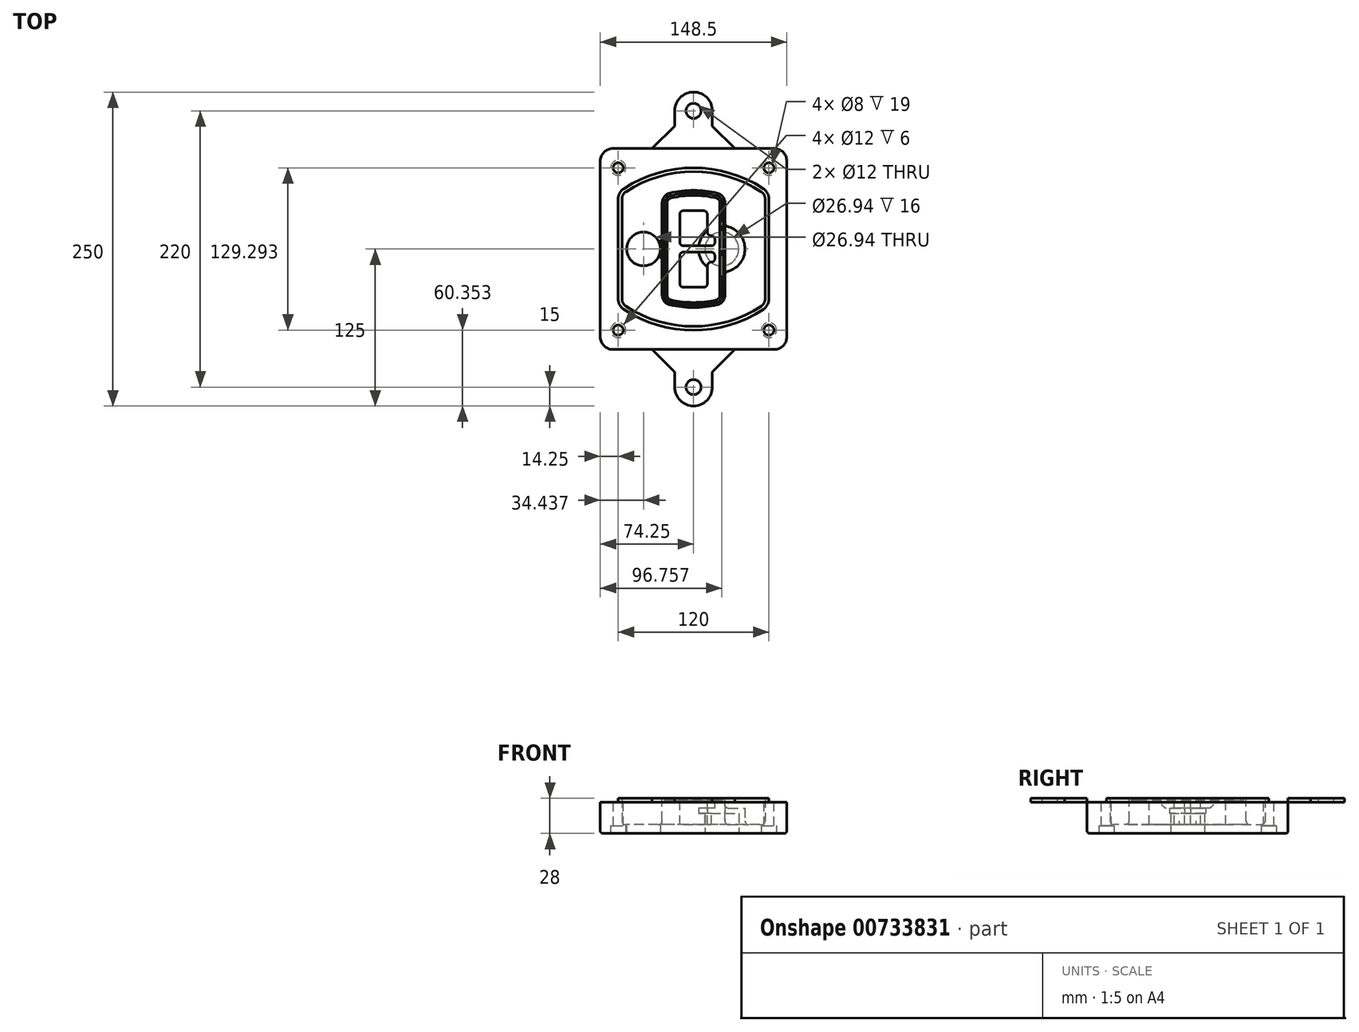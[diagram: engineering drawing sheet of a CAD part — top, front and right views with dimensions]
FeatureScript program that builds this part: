
annotation { "Feature Type Name" : "Feature", "Feature Type Description" : "" }
export const myFeature = defineFeature(function(context is Context, id is Id, definition is map)
    precondition{}
    {
        {
            var Q0;
            Q0=qCreatedBy(makeId("Top.planeOp"),FACE);
            var sketch = newSketch(context, id + "F0", { "sketchPlane" : qUnion([Q0])});
            skPoint(sketch, "E0.rect.middle", {"position": v(0, 0) * mm});
            skLineSegment(sketch, "E1.bottom", {"start": v(-64.25, -80) * mm, "end": v(64.25, -80) * mm});
            skLineSegment(sketch, "E1.top", {"start": v(-64.25, 80) * mm, "end": v(64.25, 80) * mm});
            skLineSegment(sketch, "E1.left", {"start": v(-74.25, -70) * mm, "end": v(-74.25, 70) * mm});
            skLineSegment(sketch, "E1.right", {"start": v(74.25, -70) * mm, "end": v(74.25, 70) * mm});
            skLineSegment(sketch, "E2", {"start": v(-74.25, 80) * mm, "end": v(74.25, -80) * mm, "construction": true});
            skLineSegment(sketch, "E3", {"start": v(74.25, 80) * mm, "end": v(-74.25, -80) * mm, "construction": true});
            skCircle(sketch, "E4", {"center": v(-60, 64.65) * mm, "radius": 4 * mm});
            skCircle(sketch, "E5", {"center": v(60, 64.65) * mm, "radius": 4 * mm});
            skCircle(sketch, "E6", {"center": v(60, -64.65) * mm, "radius": 4 * mm});
            skCircle(sketch, "E7", {"center": v(-60, -64.65) * mm, "radius": 4 * mm});
            skLineSegment(sketch, "E8", {"start": v(-60, 64.65) * mm, "end": v(60, 64.65) * mm, "construction": true});
            skLineSegment(sketch, "E9", {"start": v(60, 64.65) * mm, "end": v(60, -64.65) * mm, "construction": true});
            skLineSegment(sketch, "E10", {"start": v(60, -64.65) * mm, "end": v(-60, -64.65) * mm, "construction": true});
            skLineSegment(sketch, "E11", {"start": v(-60, -64.65) * mm, "end": v(-60, 64.65) * mm, "construction": true});
            skLineSegment(sketch, "E12", {"start": v(-60, 39.77) * mm, "end": v(-60, -39.77) * mm});
            skLineSegment(sketch, "E13", {"start": v(60, 39.77) * mm, "end": v(60, -39.77) * mm});
            skArc(sketch, "E14", {"start": v(55.47, 48.14) * mm, "mid": v(0, 64.65) * mm, "end": v(-55.47, 48.14) * mm});
            skArc(sketch, "E15", {"start": v(-55.47, -48.14) * mm, "mid": v(0, -64.65) * mm, "end": v(55.47, -48.14) * mm});
            skLineSegment(sketch, "E16", {"start": v(-60, 0) * mm, "end": v(60, 0) * mm, "construction": true});
            skPoint(sketch, "E17.visualSharp", {"position": v(-60, -45) * mm});
            skArc(sketch, "E17.filletArc", {"start": v(-60, -39.77) * mm, "mid": v(-58.8, -44.53) * mm, "end": v(-55.47, -48.14) * mm});
            skPoint(sketch, "E18.visualSharp", {"position": v(-60, 45) * mm});
            skArc(sketch, "E18.filletArc", {"start": v(-55.47, 48.14) * mm, "mid": v(-58.8, 44.53) * mm, "end": v(-60, 39.77) * mm});
            skPoint(sketch, "E19.visualSharp", {"position": v(60, 45) * mm});
            skArc(sketch, "E19.filletArc", {"start": v(60, 39.77) * mm, "mid": v(58.8, 44.53) * mm, "end": v(55.47, 48.14) * mm});
            skPoint(sketch, "E20.visualSharp", {"position": v(60, -45) * mm});
            skArc(sketch, "E20.filletArc", {"start": v(55.47, -48.14) * mm, "mid": v(58.8, -44.53) * mm, "end": v(60, -39.77) * mm});
            skPoint(sketch, "E21.visualSharp", {"position": v(-74.25, 80) * mm});
            skArc(sketch, "E21.filletArc", {"start": v(-64.25, 80) * mm, "mid": v(-71.32, 77.07) * mm, "end": v(-74.25, 70) * mm});
            skPoint(sketch, "E22.visualSharp", {"position": v(74.25, 80) * mm});
            skArc(sketch, "E22.filletArc", {"start": v(74.25, 70) * mm, "mid": v(71.32, 77.07) * mm, "end": v(64.25, 80) * mm});
            skPoint(sketch, "E23.visualSharp", {"position": v(74.25, -80) * mm});
            skArc(sketch, "E23.filletArc", {"start": v(64.25, -80) * mm, "mid": v(71.32, -77.07) * mm, "end": v(74.25, -70) * mm});
            skPoint(sketch, "E24.visualSharp", {"position": v(-74.25, -80) * mm});
            skArc(sketch, "E24.filletArc", {"start": v(-74.25, -70) * mm, "mid": v(-71.32, -77.07) * mm, "end": v(-64.25, -80) * mm});
            skArc(sketch, "E25.0", {"start": v(57, 39.77) * mm, "mid": v(56.16, 43.1) * mm, "end": v(53.83, 45.63) * mm});
            skLineSegment(sketch, "E25.1", {"start": v(57, 39.77) * mm, "end": v(57, -39.77) * mm});
            skArc(sketch, "E25.2", {"start": v(53.83, -45.63) * mm, "mid": v(56.16, -43.1) * mm, "end": v(57, -39.77) * mm});
            skArc(sketch, "E25.3", {"start": v(-53.83, -45.63) * mm, "mid": v(0, -61.65) * mm, "end": v(53.83, -45.63) * mm});
            skArc(sketch, "E25.4", {"start": v(-57, -39.77) * mm, "mid": v(-56.16, -43.1) * mm, "end": v(-53.83, -45.63) * mm});
            skArc(sketch, "E25.5", {"start": v(53.83, 45.63) * mm, "mid": v(0, 61.65) * mm, "end": v(-53.83, 45.63) * mm});
            skLineSegment(sketch, "E25.6", {"start": v(-57, 39.77) * mm, "end": v(-57, -39.77) * mm});
            skArc(sketch, "E25.7", {"start": v(-53.83, 45.63) * mm, "mid": v(-56.16, 43.1) * mm, "end": v(-57, 39.77) * mm});
            skArc(sketch, "E26.0", {"start": v(-57.66, 51.49) * mm, "mid": v(-62.31, 46.43) * mm, "end": v(-64, 39.77) * mm});
            skArc(sketch, "E26.1", {"start": v(57.66, 51.49) * mm, "mid": v(0, 68.65) * mm, "end": v(-57.66, 51.49) * mm});
            skArc(sketch, "E26.2", {"start": v(64, 39.77) * mm, "mid": v(62.31, 46.43) * mm, "end": v(57.66, 51.49) * mm});
            skLineSegment(sketch, "E26.3", {"start": v(64, 39.77) * mm, "end": v(64, -39.77) * mm});
            skArc(sketch, "E26.4", {"start": v(57.66, -51.49) * mm, "mid": v(62.31, -46.43) * mm, "end": v(64, -39.77) * mm});
            skLineSegment(sketch, "E26.5", {"start": v(-64, 39.77) * mm, "end": v(-64, -39.77) * mm});
            skArc(sketch, "E26.6", {"start": v(-57.66, -51.49) * mm, "mid": v(0, -68.65) * mm, "end": v(57.66, -51.49) * mm});
            skArc(sketch, "E26.7", {"start": v(-64, -39.77) * mm, "mid": v(-62.31, -46.43) * mm, "end": v(-57.66, -51.49) * mm});
            skSolve(sketch);
        }
        {
            var Q0;
            Q0=makeQuery(id+"F0.imprint","IMPRINT",FACE,{"disambiguationData":[TD([[makeQuery(id+"F0.imprint","IMPRINT",EDGE,{"derivedFrom":sQuery(id+"F0.wireOp",EDGE,"E1.bottom")}),1.0]])]});
            var Q1;
            Q1=makeQuery(id+"F0.imprint","IMPRINT",FACE,{"disambiguationData":[TD([[makeQuery(id+"F0.imprint","IMPRINT",EDGE,{"derivedFrom":sQuery(id+"F0.wireOp",EDGE,"E12")}),1.0]])]});
            var Q2;
            Q2=makeQuery(id+"F0.imprint","IMPRINT",FACE,{"disambiguationData":[TD([[makeQuery(id+"F0.imprint","IMPRINT",EDGE,{"derivedFrom":sQuery(id+"F0.wireOp",EDGE,"E25.0")}),1.0]])]});
            var Q3;
            Q3=makeQuery(id+"F0.imprint","IMPRINT",FACE,{"disambiguationData":[TD([[makeQuery(id+"F0.imprint","IMPRINT",EDGE,{"derivedFrom":sQuery(id+"F0.wireOp",EDGE,"E12")}),-1.0]])]});
            extrude(context, id + "F1", {"entities" : qUnion([Q0, Q1, Q2, Q3]), "oppositeDirection" : true, "depth" : 25 * mm});
        }
        {
            var Q0;
            Q0=makeQuery(id+"F0.imprint","IMPRINT",FACE,{"disambiguationData":[TD([[makeQuery(id+"F0.imprint","IMPRINT",EDGE,{"derivedFrom":sQuery(id+"F0.wireOp",EDGE,"E12")}),1.0]])]});
            extrude(context, id + "F2", {"entities" : qUnion([Q0]), "operationType" : NewBodyOperationType.ADD, "depth" : 3 * mm});
        }
        {
            var Q0;
            Q0=makeQuery(id+"F0.imprint","IMPRINT",FACE,{"disambiguationData":[TD([[makeQuery(id+"F0.imprint","IMPRINT",EDGE,{"derivedFrom":sQuery(id+"F0.wireOp",EDGE,"E25.0")}),1.0]])]});
            extrude(context, id + "F3", {"entities" : qUnion([Q0]), "operationType" : NewBodyOperationType.REMOVE, "oppositeDirection" : true, "depth" : 18 * mm});
        }
        {
            var Q0;
            Q0=makeQuery(id+"F2.opExtrude","CAP_FACE",FACE,{"disambiguationData":[OSD([sQuery(id+"F0.wireOp",EDGE,"E12"),sQuery(id+"F0.wireOp",EDGE,"E13"),sQuery(id+"F0.wireOp",EDGE,"E14"),sQuery(id+"F0.wireOp",EDGE,"E15"),sQuery(id+"F0.wireOp",EDGE,"E17.filletArc"),sQuery(id+"F0.wireOp",EDGE,"E18.filletArc"),sQuery(id+"F0.wireOp",EDGE,"E19.filletArc"),sQuery(id+"F0.wireOp",EDGE,"E20.filletArc"),sQuery(id+"F0.wireOp",EDGE,"E25.0"),sQuery(id+"F0.wireOp",EDGE,"E25.1"),sQuery(id+"F0.wireOp",EDGE,"E25.2"),sQuery(id+"F0.wireOp",EDGE,"E25.3"),sQuery(id+"F0.wireOp",EDGE,"E25.4"),sQuery(id+"F0.wireOp",EDGE,"E25.5"),sQuery(id+"F0.wireOp",EDGE,"E25.6"),sQuery(id+"F0.wireOp",EDGE,"E25.7")])],"isStart":false});
            var sketch = newSketch(context, id + "F4", { "sketchPlane" : qUnion([Q0])});
            skArc(sketch, "E27.0", {"start": v(-18.8, -44.5) * mm, "mid": v(0, -46.65) * mm, "end": v(18.8, -44.5) * mm});
            skArc(sketch, "E28.0", {"start": v(18.8, 44.5) * mm, "mid": v(0, 46.65) * mm, "end": v(-18.8, 44.5) * mm});
            skLineSegment(sketch, "E29", {"start": v(-25, 36.7) * mm, "end": v(-25, -36.7) * mm});
            skLineSegment(sketch, "E30", {"start": v(25, 36.7) * mm, "end": v(25, -36.7) * mm});
            skLineSegment(sketch, "E31", {"start": v(-25, 42.81) * mm, "end": v(25, 42.81) * mm, "construction": true});
            skLineSegment(sketch, "E32", {"start": v(-25, -42.81) * mm, "end": v(25, -42.81) * mm, "construction": true});
            skPoint(sketch, "E33.visualSharp", {"position": v(-25, 42.81) * mm});
            skArc(sketch, "E33.filletArc", {"start": v(-18.8, 44.5) * mm, "mid": v(-23.26, 41.69) * mm, "end": v(-25, 36.7) * mm});
            skPoint(sketch, "E34.visualSharp", {"position": v(25, 42.81) * mm});
            skArc(sketch, "E34.filletArc", {"start": v(25, 36.7) * mm, "mid": v(23.26, 41.69) * mm, "end": v(18.8, 44.5) * mm});
            skPoint(sketch, "E35.visualSharp", {"position": v(25, -42.81) * mm});
            skArc(sketch, "E35.filletArc", {"start": v(18.8, -44.5) * mm, "mid": v(23.26, -41.69) * mm, "end": v(25, -36.7) * mm});
            skPoint(sketch, "E36.visualSharp", {"position": v(-25, -42.81) * mm});
            skArc(sketch, "E36.filletArc", {"start": v(-25, -36.7) * mm, "mid": v(-23.26, -41.69) * mm, "end": v(-18.8, -44.5) * mm});
            skArc(sketch, "E37.0", {"start": v(53.83, 45.63) * mm, "mid": v(0, 61.65) * mm, "end": v(-53.83, 45.63) * mm});
            skArc(sketch, "E37.1", {"start": v(-53.83, 45.63) * mm, "mid": v(-56.16, 43.1) * mm, "end": v(-57, 39.77) * mm});
            skLineSegment(sketch, "E37.2", {"start": v(-57, 39.77) * mm, "end": v(-57, -39.77) * mm});
            skArc(sketch, "E37.3", {"start": v(-57, -39.77) * mm, "mid": v(-56.16, -43.1) * mm, "end": v(-53.83, -45.63) * mm});
            skArc(sketch, "E37.4", {"start": v(-53.83, -45.63) * mm, "mid": v(0, -61.65) * mm, "end": v(53.83, -45.63) * mm});
            skArc(sketch, "E37.5", {"start": v(53.83, -45.63) * mm, "mid": v(56.16, -43.1) * mm, "end": v(57, -39.77) * mm});
            skLineSegment(sketch, "E37.6", {"start": v(57, 39.77) * mm, "end": v(57, -39.77) * mm});
            skArc(sketch, "E37.7", {"start": v(57, 39.77) * mm, "mid": v(56.16, 43.1) * mm, "end": v(53.83, 45.63) * mm});
            skLineSegment(sketch, "E38.0", {"start": v(23, 36.7) * mm, "end": v(23, -36.7) * mm});
            skArc(sketch, "E38.1", {"start": v(18.35, -42.55) * mm, "mid": v(21.7, -40.44) * mm, "end": v(23, -36.7) * mm});
            skArc(sketch, "E38.2", {"start": v(-18.35, -42.55) * mm, "mid": v(0, -44.65) * mm, "end": v(18.35, -42.55) * mm});
            skArc(sketch, "E38.3", {"start": v(-23, -36.7) * mm, "mid": v(-21.7, -40.44) * mm, "end": v(-18.35, -42.55) * mm});
            skLineSegment(sketch, "E38.4", {"start": v(-23, 36.7) * mm, "end": v(-23, -36.7) * mm});
            skArc(sketch, "E38.5", {"start": v(23, 36.7) * mm, "mid": v(21.7, 40.44) * mm, "end": v(18.35, 42.55) * mm});
            skArc(sketch, "E38.6", {"start": v(-18.35, 42.55) * mm, "mid": v(-21.7, 40.44) * mm, "end": v(-23, 36.7) * mm});
            skArc(sketch, "E38.7", {"start": v(18.35, 42.55) * mm, "mid": v(0, 44.65) * mm, "end": v(-18.35, 42.55) * mm});
            skArc(sketch, "E39.0", {"start": v(21, 36.7) * mm, "mid": v(20.13, 39.2) * mm, "end": v(17.9, 40.6) * mm});
            skLineSegment(sketch, "E39.1", {"start": v(21, 36.7) * mm, "end": v(21, -36.7) * mm});
            skArc(sketch, "E39.2", {"start": v(17.9, -40.6) * mm, "mid": v(20.13, -39.2) * mm, "end": v(21, -36.7) * mm});
            skArc(sketch, "E39.3", {"start": v(-17.9, -40.6) * mm, "mid": v(0, -42.65) * mm, "end": v(17.9, -40.6) * mm});
            skArc(sketch, "E39.4", {"start": v(-21, -36.7) * mm, "mid": v(-20.13, -39.2) * mm, "end": v(-17.9, -40.6) * mm});
            skArc(sketch, "E39.5", {"start": v(17.9, 40.6) * mm, "mid": v(0, 42.65) * mm, "end": v(-17.9, 40.6) * mm});
            skLineSegment(sketch, "E39.6", {"start": v(-21, 36.7) * mm, "end": v(-21, -36.7) * mm});
            skArc(sketch, "E39.7", {"start": v(-17.9, 40.6) * mm, "mid": v(-20.13, 39.2) * mm, "end": v(-21, 36.7) * mm});
            skLineSegment(sketch, "E40", {"start": v(-25, 0) * mm, "end": v(25, 0) * mm, "construction": true});
            skLineSegment(sketch, "E41", {"start": v(-11, 5.5) * mm, "end": v(-11, 27.5) * mm});
            skLineSegment(sketch, "E42", {"start": v(-8, 30.5) * mm, "end": v(8, 30.5) * mm});
            skLineSegment(sketch, "E43", {"start": v(11, 27.5) * mm, "end": v(11, 13.5) * mm});
            skLineSegment(sketch, "E44", {"start": v(14, 10.5) * mm, "end": v(14, 10.5) * mm});
            skLineSegment(sketch, "E45", {"start": v(17, 7.5) * mm, "end": v(17, 5.5) * mm});
            skLineSegment(sketch, "E46", {"start": v(14, 2.5) * mm, "end": v(-8, 2.5) * mm});
            skPoint(sketch, "E47.visualSharp", {"position": v(-11, 30.5) * mm});
            skArc(sketch, "E47.filletArc", {"start": v(-8, 30.5) * mm, "mid": v(-10.12, 29.62) * mm, "end": v(-11, 27.5) * mm});
            skPoint(sketch, "E48.visualSharp", {"position": v(11, 30.5) * mm});
            skArc(sketch, "E48.filletArc", {"start": v(11, 27.5) * mm, "mid": v(10.12, 29.62) * mm, "end": v(8, 30.5) * mm});
            skPoint(sketch, "E49.visualSharp", {"position": v(11, 10.5) * mm});
            skArc(sketch, "E49.filletArc", {"start": v(11, 13.5) * mm, "mid": v(11.88, 11.38) * mm, "end": v(14, 10.5) * mm});
            skPoint(sketch, "E50.visualSharp", {"position": v(17, 10.5) * mm});
            skArc(sketch, "E50.filletArc", {"start": v(17, 7.5) * mm, "mid": v(16.12, 9.62) * mm, "end": v(14, 10.5) * mm});
            skPoint(sketch, "E51.visualSharp", {"position": v(17, 2.5) * mm});
            skArc(sketch, "E51.filletArc", {"start": v(14, 2.5) * mm, "mid": v(16.12, 3.38) * mm, "end": v(17, 5.5) * mm});
            skPoint(sketch, "E52.visualSharp", {"position": v(-11, 2.5) * mm});
            skArc(sketch, "E52.filletArc", {"start": v(-11, 5.5) * mm, "mid": v(-10.12, 3.38) * mm, "end": v(-8, 2.5) * mm});
            skLineSegment(sketch, "E53.0.MirrorCS", {"start": v(14, -2.5) * mm, "end": v(-8, -2.5) * mm});
            skArc(sketch, "E54.0.MirrorCS", {"start": v(-11, -5.5) * mm, "mid": v(-10.12, -3.38) * mm, "end": v(-8, -2.5) * mm});
            skLineSegment(sketch, "E55.0.MirrorCS", {"start": v(-11, -5.5) * mm, "end": v(-11, -27.5) * mm});
            skArc(sketch, "E56.0.MirrorCS", {"start": v(-8, -30.5) * mm, "mid": v(-10.12, -29.62) * mm, "end": v(-11, -27.5) * mm});
            skLineSegment(sketch, "E57.0.MirrorCS", {"start": v(-8, -30.5) * mm, "end": v(8, -30.5) * mm});
            skArc(sketch, "E58.0.MirrorCS", {"start": v(11, -27.5) * mm, "mid": v(10.12, -29.62) * mm, "end": v(8, -30.5) * mm});
            skLineSegment(sketch, "E59.0.MirrorCS", {"start": v(11, -27.5) * mm, "end": v(11, -13.5) * mm});
            skArc(sketch, "E60.0.MirrorCS", {"start": v(11, -13.5) * mm, "mid": v(11.88, -11.38) * mm, "end": v(14, -10.5) * mm});
            skArc(sketch, "E61.0.MirrorCS", {"start": v(17, -7.5) * mm, "mid": v(16.12, -9.62) * mm, "end": v(14, -10.5) * mm});
            skLineSegment(sketch, "E62.0.MirrorCS", {"start": v(17, -7.5) * mm, "end": v(17, -5.5) * mm});
            skArc(sketch, "E63.0.MirrorCS", {"start": v(14, -2.5) * mm, "mid": v(16.12, -3.38) * mm, "end": v(17, -5.5) * mm});
            skSolve(sketch);
        }
        {
            var Q0;
            Q0=makeQuery(id+"F4.imprint","IMPRINT",FACE,{"disambiguationData":[TD([[makeQuery(id+"F4.imprint","IMPRINT",EDGE,{"derivedFrom":sQuery(id+"F4.wireOp",EDGE,"E27.0")}),1.0]])]});
            var Q1;
            Q1=makeQuery(id+"F4.imprint","IMPRINT",FACE,{"disambiguationData":[TD([[makeQuery(id+"F4.imprint","IMPRINT",EDGE,{"derivedFrom":sQuery(id+"F4.wireOp",EDGE,"E38.0")}),-1.0]])]});
            var Q2;
            Q2=makeQuery(id+"F4.imprint","IMPRINT",FACE,{"disambiguationData":[TD([[makeQuery(id+"F4.imprint","IMPRINT",EDGE,{"derivedFrom":sQuery(id+"F4.wireOp",EDGE,"E39.0")}),1.0]])]});
            extrude(context, id + "F5", {"entities" : qUnion([Q0, Q1, Q2]), "operationType" : NewBodyOperationType.ADD, "endBound" : BoundingType.UP_TO_NEXT, "oppositeDirection" : true, "depth" : 25 * mm});
        }
        {
            var Q0;
            Q0=makeQuery(id+"F4.imprint","IMPRINT",FACE,{"disambiguationData":[TD([[makeQuery(id+"F4.imprint","IMPRINT",EDGE,{"derivedFrom":sQuery(id+"F4.wireOp",EDGE,"E38.0")}),-1.0]])]});
            extrude(context, id + "F6", {"entities" : qUnion([Q0]), "operationType" : NewBodyOperationType.REMOVE, "oppositeDirection" : true, "depth" : 2 * mm});
        }
        {
            var Q0;
            Q0=makeQuery(id+"F1.opExtrude","CAP_FACE",FACE,{"disambiguationData":[OSD([sQuery(id+"F0.wireOp",EDGE,"E1.bottom"),sQuery(id+"F0.wireOp",EDGE,"E1.top"),sQuery(id+"F0.wireOp",EDGE,"E1.left"),sQuery(id+"F0.wireOp",EDGE,"E1.right"),sQuery(id+"F0.wireOp",EDGE,"E4"),sQuery(id+"F0.wireOp",EDGE,"E5"),sQuery(id+"F0.wireOp",EDGE,"E6"),sQuery(id+"F0.wireOp",EDGE,"E7"),sQuery(id+"F0.wireOp",EDGE,"E21.filletArc"),sQuery(id+"F0.wireOp",EDGE,"E22.filletArc"),sQuery(id+"F0.wireOp",EDGE,"E23.filletArc"),sQuery(id+"F0.wireOp",EDGE,"E24.filletArc")])],"isStart":false});
            var sketch = newSketch(context, id + "F7", { "sketchPlane" : qUnion([Q0])});
            skCircle(sketch, "E64", {"center": v(22.5, 0) * mm, "radius": 13.47 * mm});
            skCircle(sketch, "E65", {"center": v(-39.81, 0) * mm, "radius": 13.47 * mm});
            skLineSegment(sketch, "E66", {"start": v(74.25, 0) * mm, "end": v(-74.25, 0) * mm});
            skCircle(sketch, "E67", {"center": v(22.5, 0) * mm, "radius": 18.47 * mm});
            skCircle(sketch, "E68", {"center": v(60, -64.65) * mm, "radius": 6 * mm});
            skCircle(sketch, "E69", {"center": v(-60, -64.65) * mm, "radius": 6 * mm});
            skCircle(sketch, "E70", {"center": v(-60, 64.65) * mm, "radius": 6 * mm});
            skCircle(sketch, "E71", {"center": v(60, 64.65) * mm, "radius": 6 * mm});
            skSolve(sketch);
        }
        {
            var Q0;
            {var subQ1=sQuery(id+"F7.wireOp",EDGE,"E66");var subQ4=sQuery(id+"F7.wireOp",EDGE,"E64");var subQ6=makeQuery(id+"F7.imprint","INTERSECT",VERTEX,{"disambiguationData":[OD(0.0)],"derivedFrom":[subQ4,subQ1]});Q0=makeQuery(id+"F7.imprint","IMPRINT",FACE,{"disambiguationData":[TD([[makeQuery(id+"F7.imprint","IMPRINT",EDGE,{"disambiguationData":[TD([[subQ6,-1.0]])],"derivedFrom":subQ4}),-1.0]])]});}
            var Q1;
            {var subQ0=sQuery(id+"F7.wireOp",EDGE,"E66");var subQ1=sQuery(id+"F7.wireOp",EDGE,"E64");var subQ3=makeQuery(id+"F7.imprint","INTERSECT",VERTEX,{"disambiguationData":[OD(0.0)],"derivedFrom":[subQ1,subQ0]});Q1=makeQuery(id+"F7.imprint","IMPRINT",FACE,{"disambiguationData":[TD([[makeQuery(id+"F7.imprint","IMPRINT",EDGE,{"disambiguationData":[TD([[subQ3,-1.0]])],"derivedFrom":subQ1}),1.0]])]});}
            var Q2;
            {var subQ0=sQuery(id+"F7.wireOp",EDGE,"E66");var subQ1=sQuery(id+"F7.wireOp",EDGE,"E64");var subQ3=makeQuery(id+"F7.imprint","INTERSECT",VERTEX,{"disambiguationData":[OD(0.0)],"derivedFrom":[subQ1,subQ0]});Q2=makeQuery(id+"F7.imprint","IMPRINT",FACE,{"disambiguationData":[TD([[makeQuery(id+"F7.imprint","IMPRINT",EDGE,{"disambiguationData":[TD([[subQ3,1.0]])],"derivedFrom":subQ1}),1.0]])]});}
            var Q3;
            {var subQ1=sQuery(id+"F7.wireOp",EDGE,"E66");var subQ4=sQuery(id+"F7.wireOp",EDGE,"E64");var subQ6=makeQuery(id+"F7.imprint","INTERSECT",VERTEX,{"disambiguationData":[OD(0.0)],"derivedFrom":[subQ4,subQ1]});Q3=makeQuery(id+"F7.imprint","IMPRINT",FACE,{"disambiguationData":[TD([[makeQuery(id+"F7.imprint","IMPRINT",EDGE,{"disambiguationData":[TD([[subQ6,1.0]])],"derivedFrom":subQ4}),-1.0]])]});}
            extrude(context, id + "F8", {"entities" : qUnion([Q0, Q1, Q2, Q3]), "operationType" : NewBodyOperationType.ADD, "oppositeDirection" : true, "depth" : 20 * mm});
        }
        {
            var Q0;
            {var subQ0=sQuery(id+"F7.wireOp",EDGE,"E66");var subQ1=sQuery(id+"F7.wireOp",EDGE,"E64");var subQ3=makeQuery(id+"F7.imprint","INTERSECT",VERTEX,{"disambiguationData":[OD(0.0)],"derivedFrom":[subQ1,subQ0]});Q0=makeQuery(id+"F7.imprint","IMPRINT",FACE,{"disambiguationData":[TD([[makeQuery(id+"F7.imprint","IMPRINT",EDGE,{"disambiguationData":[TD([[subQ3,-1.0]])],"derivedFrom":subQ1}),1.0]])]});}
            var Q1;
            {var subQ0=sQuery(id+"F7.wireOp",EDGE,"E66");var subQ1=sQuery(id+"F7.wireOp",EDGE,"E64");var subQ3=makeQuery(id+"F7.imprint","INTERSECT",VERTEX,{"disambiguationData":[OD(0.0)],"derivedFrom":[subQ1,subQ0]});Q1=makeQuery(id+"F7.imprint","IMPRINT",FACE,{"disambiguationData":[TD([[makeQuery(id+"F7.imprint","IMPRINT",EDGE,{"disambiguationData":[TD([[subQ3,1.0]])],"derivedFrom":subQ1}),1.0]])]});}
            extrude(context, id + "F9", {"entities" : qUnion([Q0, Q1]), "operationType" : NewBodyOperationType.REMOVE, "oppositeDirection" : true, "depth" : 16 * mm});
        }
        {
            var Q0;
            {var subQ0=sQuery(id+"F7.wireOp",EDGE,"E66");var subQ1=sQuery(id+"F7.wireOp",EDGE,"E65");var subQ3=makeQuery(id+"F7.imprint","INTERSECT",VERTEX,{"disambiguationData":[OD(0.0)],"derivedFrom":[subQ1,subQ0]});Q0=makeQuery(id+"F7.imprint","IMPRINT",FACE,{"disambiguationData":[TD([[makeQuery(id+"F7.imprint","IMPRINT",EDGE,{"disambiguationData":[TD([[subQ3,-1.0]])],"derivedFrom":subQ1}),1.0]])]});}
            var Q1;
            {var subQ0=sQuery(id+"F7.wireOp",EDGE,"E66");var subQ1=sQuery(id+"F7.wireOp",EDGE,"E65");var subQ3=makeQuery(id+"F7.imprint","INTERSECT",VERTEX,{"disambiguationData":[OD(0.0)],"derivedFrom":[subQ1,subQ0]});Q1=makeQuery(id+"F7.imprint","IMPRINT",FACE,{"disambiguationData":[TD([[makeQuery(id+"F7.imprint","IMPRINT",EDGE,{"disambiguationData":[TD([[subQ3,1.0]])],"derivedFrom":subQ1}),1.0]])]});}
            extrude(context, id + "F10", {"entities" : qUnion([Q0, Q1]), "operationType" : NewBodyOperationType.REMOVE, "oppositeDirection" : true, "depth" : 25 * mm});
        }
        {
            var Q0;
            Q0=makeQuery(id+"F7.imprint","IMPRINT",FACE,{"disambiguationData":[TD([[makeQuery(id+"F7.imprint","IMPRINT",EDGE,{"derivedFrom":sQuery(id+"F7.wireOp",EDGE,"E68")}),1.0]])]});
            var Q1;
            Q1=makeQuery(id+"F7.imprint","IMPRINT",FACE,{"disambiguationData":[TD([[makeQuery(id+"F7.imprint","IMPRINT",EDGE,{"derivedFrom":makeQuery(id+"F1.opExtrude","CAP_EDGE",EDGE,{"disambiguationData":[OSD([sQuery(id+"F0.wireOp",EDGE,"E5")])],"isStart":false})}),-1.0]])]});
            var Q2;
            Q2=makeQuery(id+"F7.imprint","IMPRINT",FACE,{"disambiguationData":[TD([[makeQuery(id+"F7.imprint","IMPRINT",EDGE,{"derivedFrom":sQuery(id+"F7.wireOp",EDGE,"E69")}),1.0]])]});
            var Q3;
            Q3=makeQuery(id+"F7.imprint","IMPRINT",FACE,{"disambiguationData":[TD([[makeQuery(id+"F7.imprint","IMPRINT",EDGE,{"derivedFrom":makeQuery(id+"F1.opExtrude","CAP_EDGE",EDGE,{"disambiguationData":[OSD([sQuery(id+"F0.wireOp",EDGE,"E4")])],"isStart":false})}),-1.0]])]});
            var Q4;
            Q4=makeQuery(id+"F7.imprint","IMPRINT",FACE,{"disambiguationData":[TD([[makeQuery(id+"F7.imprint","IMPRINT",EDGE,{"derivedFrom":sQuery(id+"F7.wireOp",EDGE,"E70")}),1.0]])]});
            var Q5;
            Q5=makeQuery(id+"F7.imprint","IMPRINT",FACE,{"disambiguationData":[TD([[makeQuery(id+"F7.imprint","IMPRINT",EDGE,{"derivedFrom":makeQuery(id+"F1.opExtrude","CAP_EDGE",EDGE,{"disambiguationData":[OSD([sQuery(id+"F0.wireOp",EDGE,"E7")])],"isStart":false})}),-1.0]])]});
            var Q6;
            Q6=makeQuery(id+"F7.imprint","IMPRINT",FACE,{"disambiguationData":[TD([[makeQuery(id+"F7.imprint","IMPRINT",EDGE,{"derivedFrom":sQuery(id+"F7.wireOp",EDGE,"E71")}),1.0]])]});
            var Q7;
            Q7=makeQuery(id+"F7.imprint","IMPRINT",FACE,{"disambiguationData":[TD([[makeQuery(id+"F7.imprint","IMPRINT",EDGE,{"derivedFrom":makeQuery(id+"F1.opExtrude","CAP_EDGE",EDGE,{"disambiguationData":[OSD([sQuery(id+"F0.wireOp",EDGE,"E6")])],"isStart":false})}),-1.0]])]});
            extrude(context, id + "F11", {"entities" : qUnion([Q0, Q1, Q2, Q3, Q4, Q5, Q6, Q7]), "operationType" : NewBodyOperationType.REMOVE, "oppositeDirection" : true, "depth" : 6 * mm});
        }
        {
            var Q0;
            Q0=makeQuery(id+"F9.boolean.opBoolean","COPY",FACE,{"derivedFrom":makeQuery(id+"F9.opExtrude","CAP_FACE",FACE,{"disambiguationData":[OSD([sQuery(id+"F7.wireOp",EDGE,"E64")])],"isStart":false})});
            var sketch = newSketch(context, id + "F12", { "sketchPlane" : qUnion([Q0])});
            skArc(sketch, "E72.0", {"start": v(11, 14.45) * mm, "mid": v(6.45, 9.13) * mm, "end": v(4.2, 2.5) * mm});
            skArc(sketch, "E72.1", {"start": v(4.2, -2.5) * mm, "mid": v(6.45, -9.13) * mm, "end": v(11, -14.45) * mm});
            skLineSegment(sketch, "E73", {"start": v(4.2, -2.5) * mm, "end": v(14, -2.5) * mm});
            skLineSegment(sketch, "E74.0", {"start": v(14, 2.5) * mm, "end": v(4.2, 2.5) * mm});
            skArc(sketch, "E74.1", {"start": v(14, 2.5) * mm, "mid": v(16.12, 3.38) * mm, "end": v(17, 5.5) * mm});
            skLineSegment(sketch, "E74.2", {"start": v(17, 7.5) * mm, "end": v(17, 5.5) * mm});
            skArc(sketch, "E74.3", {"start": v(17, 7.5) * mm, "mid": v(16.12, 9.62) * mm, "end": v(14, 10.5) * mm});
            skArc(sketch, "E74.4", {"start": v(11, 13.5) * mm, "mid": v(11.88, 11.38) * mm, "end": v(14, 10.5) * mm});
            skLineSegment(sketch, "E74.5", {"start": v(11, 14.45) * mm, "end": v(11, 13.5) * mm});
            skLineSegment(sketch, "E74.7", {"start": v(14, -2.5) * mm, "end": v(4.2, -2.5) * mm});
            skArc(sketch, "E74.8", {"start": v(14, -2.5) * mm, "mid": v(16.12, -3.38) * mm, "end": v(17, -5.5) * mm});
            skLineSegment(sketch, "E74.9", {"start": v(17, -7.5) * mm, "end": v(17, -5.5) * mm});
            skArc(sketch, "E74.10", {"start": v(17, -7.5) * mm, "mid": v(16.12, -9.62) * mm, "end": v(14, -10.5) * mm});
            skArc(sketch, "E74.11", {"start": v(11, -13.5) * mm, "mid": v(11.88, -11.38) * mm, "end": v(14, -10.5) * mm});
            skLineSegment(sketch, "E74.12", {"start": v(11, -14.45) * mm, "end": v(11, -13.5) * mm});
            skPoint(sketch, "E75.orphan", {"position": v(11, -27.5) * mm});
            skPoint(sketch, "E76.orphan", {"position": v(-8, -2.5) * mm});
            skPoint(sketch, "E77.orphan", {"position": v(-8, 2.5) * mm});
            skPoint(sketch, "E78.orphan", {"position": v(11, 27.5) * mm});
            skSolve(sketch);
        }
        {
            var Q0;
            {var subQ7=sQuery(id+"F12.wireOp",EDGE,"E72.0");var subQ14=sQuery(id+"F12.wireOp",EDGE,"E72.1");var subQ16=sQuery(id+"F12.wireOp",EDGE,"E74.1");var subQ18=sQuery(id+"F12.wireOp",EDGE,"E74.8");Q0=qUnion([makeQuery(id+"F12.imprint","IMPRINT",FACE,{"disambiguationData":[TD([[makeQuery(id+"F12.imprint","IMPRINT",EDGE,{"derivedFrom":subQ7}),1.0]])]}),makeQuery(id+"F12.imprint","IMPRINT",FACE,{"disambiguationData":[TD([[makeQuery(id+"F12.imprint","IMPRINT",EDGE,{"derivedFrom":subQ14}),1.0]])]}),makeQuery(id+"F12.imprint","IMPRINT",FACE,{"disambiguationData":[TD([[makeQuery(id+"F12.imprint","IMPRINT",EDGE,{"derivedFrom":subQ16}),1.0]])]}),makeQuery(id+"F12.imprint","IMPRINT",FACE,{"disambiguationData":[TD([[makeQuery(id+"F12.imprint","IMPRINT",EDGE,{"derivedFrom":subQ18}),-1.0]])]})]);}
            var Q1;
            Q1=makeQuery(id+"F5.boolean.opBoolean","SPLIT",FACE,{"disambiguationData":[TD([makeQuery(id+"F5.opExtrude","SWEPT_FACE",FACE,{"disambiguationData":[OSD([sQuery(id+"F4.wireOp",EDGE,"E41")])]})])],"derivedFrom":makeQuery(id+"F3.boolean.opBoolean","COPY",FACE,{"derivedFrom":makeQuery(id+"F3.opExtrude","CAP_FACE",FACE,{"disambiguationData":[OSD([sQuery(id+"F0.wireOp",EDGE,"E25.0"),sQuery(id+"F0.wireOp",EDGE,"E25.1"),sQuery(id+"F0.wireOp",EDGE,"E25.2"),sQuery(id+"F0.wireOp",EDGE,"E25.3"),sQuery(id+"F0.wireOp",EDGE,"E25.4"),sQuery(id+"F0.wireOp",EDGE,"E25.5"),sQuery(id+"F0.wireOp",EDGE,"E25.6"),sQuery(id+"F0.wireOp",EDGE,"E25.7")])],"isStart":false})})});
            extrude(context, id + "F13", {"entities" : qUnion([Q0]), "operationType" : NewBodyOperationType.REMOVE, "endBound" : BoundingType.UP_TO_SURFACE, "endBoundEntityFace" : qUnion([Q1]), "depth" : 25 * mm});
        }
        {
            var Q0;
            Q0=makeQuery(id+"F3.boolean.opBoolean","COPY",EDGE,{"derivedFrom":makeQuery(id+"F3.opExtrude","CAP_EDGE",EDGE,{"disambiguationData":[OSD([sQuery(id+"F0.wireOp",EDGE,"E25.6")])],"isStart":false})});
            var Q1;
            Q1=makeQuery(id+"F8.boolean.opBoolean","INTERSECT",EDGE,{"derivedFrom":[makeQuery(id+"F5.opExtrude","SWEPT_FACE",FACE,{"disambiguationData":[OSD([sQuery(id+"F4.wireOp",EDGE,"E30")])]}),makeQuery(id+"F8.opExtrude","CAP_FACE",FACE,{"disambiguationData":[OSD([sQuery(id+"F7.wireOp",EDGE,"E67")])],"isStart":false})]});
            var Q2;
            Q2=makeQuery(id+"F8.boolean.opBoolean","INTERSECT",EDGE,{"disambiguationData":[OD(1.0)],"derivedFrom":[makeQuery(id+"F5.opExtrude","SWEPT_FACE",FACE,{"disambiguationData":[OSD([sQuery(id+"F4.wireOp",EDGE,"E30")])]}),makeQuery(id+"F8.opExtrude","SWEPT_FACE",FACE,{"disambiguationData":[OSD([sQuery(id+"F7.wireOp",EDGE,"E67")])]})]});
            var Q3;
            {var subQ0=sQuery(id+"F4.wireOp",EDGE,"E30");Q3=makeQuery(id+"F8.boolean.opBoolean","SPLIT",EDGE,{"disambiguationData":[TD([makeQuery(id+"F5.opExtrude","SWEPT_FACE",FACE,{"disambiguationData":[OSD([sQuery(id+"F4.wireOp",EDGE,"E35.filletArc")])]})])],"derivedFrom":makeQuery(id+"F5.opExtrude","CAP_EDGE",EDGE,{"disambiguationData":[OSD([subQ0])],"isStart":false})});}
            var Q4;
            {var subQ0=sQuery(id+"F0.wireOp",EDGE,"E25.7");var subQ1=sQuery(id+"F0.wireOp",EDGE,"E25.1");var subQ2=sQuery(id+"F0.wireOp",EDGE,"E25.6");var subQ3=sQuery(id+"F0.wireOp",EDGE,"E25.5");var subQ4=sQuery(id+"F0.wireOp",EDGE,"E25.4");var subQ5=sQuery(id+"F0.wireOp",EDGE,"E25.0");var subQ6=sQuery(id+"F0.wireOp",EDGE,"E25.2");var subQ7=sQuery(id+"F0.wireOp",EDGE,"E25.3");Q4=makeQuery(id+"F8.boolean.opBoolean","INTERSECT",EDGE,{"derivedFrom":[makeQuery(id+"F5.boolean.opBoolean","SPLIT",FACE,{"disambiguationData":[TD([makeQuery(id+"F2.opExtrude","SWEPT_FACE",FACE,{"disambiguationData":[OSD([subQ5])]})])],"derivedFrom":makeQuery(id+"F3.boolean.opBoolean","COPY",FACE,{"derivedFrom":makeQuery(id+"F3.opExtrude","CAP_FACE",FACE,{"disambiguationData":[OSD([subQ5,subQ1,subQ6,subQ7,subQ4,subQ3,subQ2,subQ0])],"isStart":false})})}),makeQuery(id+"F8.opExtrude","SWEPT_FACE",FACE,{"disambiguationData":[OSD([sQuery(id+"F7.wireOp",EDGE,"E67")])]})]});}
            var Q5;
            Q5=makeQuery(id+"F8.boolean.opBoolean","INTERSECT",EDGE,{"disambiguationData":[OD(0.0)],"derivedFrom":[makeQuery(id+"F5.opExtrude","SWEPT_FACE",FACE,{"disambiguationData":[OSD([sQuery(id+"F4.wireOp",EDGE,"E30")])]}),makeQuery(id+"F8.opExtrude","SWEPT_FACE",FACE,{"disambiguationData":[OSD([sQuery(id+"F7.wireOp",EDGE,"E67")])]})]});
            fillet(context, id + "F14", {"entities" : qUnion([Q0, Q1, Q2, Q3, Q4, Q5]), "radius" : 3 * mm, "tangentPropagation" : true, "allowEdgeOverflow" : false});
        }
        {
            var Q0;
            Q0=makeQuery(id+"F1.opExtrude","CAP_EDGE",EDGE,{"disambiguationData":[OSD([sQuery(id+"F0.wireOp",EDGE,"E1.bottom")])],"isStart":false});
            fillet(context, id + "F15", {"entities" : qUnion([Q0]), "radius" : 2 * mm, "tangentPropagation" : true, "allowEdgeOverflow" : false});
        }
        {
            var Q0;
            {var subQ0=sQuery(id+"F0.wireOp",EDGE,"E21.filletArc");var subQ1=sQuery(id+"F0.wireOp",EDGE,"E7");var subQ2=sQuery(id+"F0.wireOp",EDGE,"E6");var subQ3=sQuery(id+"F0.wireOp",EDGE,"E5");var subQ4=sQuery(id+"F0.wireOp",EDGE,"E4");var subQ5=sQuery(id+"F0.wireOp",EDGE,"E22.filletArc");var subQ6=sQuery(id+"F0.wireOp",EDGE,"E1.bottom");var subQ7=sQuery(id+"F0.wireOp",EDGE,"E1.right");var subQ8=sQuery(id+"F0.wireOp",EDGE,"E1.top");var subQ9=sQuery(id+"F0.wireOp",EDGE,"E1.left");var subQ10=sQuery(id+"F0.wireOp",EDGE,"E23.filletArc");var subQ11=sQuery(id+"F0.wireOp",EDGE,"E24.filletArc");Q0=makeQuery(id+"F2.boolean.opBoolean","SPLIT",FACE,{"disambiguationData":[TD([makeQuery(id+"F1.opExtrude","SWEPT_FACE",FACE,{"disambiguationData":[OSD([subQ6])]})])],"derivedFrom":makeQuery(id+"F1.opExtrude","CAP_FACE",FACE,{"disambiguationData":[OSD([subQ6,subQ8,subQ9,subQ7,subQ4,subQ3,subQ2,subQ1,subQ0,subQ5,subQ10,subQ11])],"isStart":true})});}
            var sketch = newSketch(context, id + "F16", { "sketchPlane" : qUnion([Q0])});
            skLineSegment(sketch, "E79", {"start": v(0, 80) * mm, "end": v(0, 111.33) * mm, "construction": true});
            skCircle(sketch, "E80", {"center": v(0, 110) * mm, "radius": 6 * mm});
            skPoint(sketch, "E81", {"position": v(-15, 110) * mm});
            skPoint(sketch, "E82", {"position": v(15, 110) * mm});
            skArc(sketch, "E83", {"start": v(15, 110) * mm, "mid": v(0, 125) * mm, "end": v(-15, 110) * mm});
            skLineSegment(sketch, "E84", {"start": v(-15, 110) * mm, "end": v(-15, 98) * mm});
            skLineSegment(sketch, "E85", {"start": v(15, 110) * mm, "end": v(15, 98) * mm});
            skLineSegment(sketch, "E86.0", {"start": v(-64.25, 80) * mm, "end": v(64.25, 80) * mm});
            skLineSegment(sketch, "E87", {"start": v(-15, 98) * mm, "end": v(-33, 80) * mm});
            skLineSegment(sketch, "E88", {"start": v(15, 98) * mm, "end": v(33, 80) * mm});
            skLineSegment(sketch, "E89", {"start": v(-74.25, 0) * mm, "end": v(74.25, 0) * mm, "construction": true});
            skLineSegment(sketch, "E90.MirrorCS", {"start": v(-15, -98) * mm, "end": v(-33, -80) * mm});
            skLineSegment(sketch, "E91.MirrorCS", {"start": v(-15, -110) * mm, "end": v(-15, -98) * mm});
            skArc(sketch, "E92.MirrorCS", {"start": v(15, -110) * mm, "mid": v(0, -125) * mm, "end": v(-15, -110) * mm});
            skLineSegment(sketch, "E93.MirrorCS", {"start": v(15, -110) * mm, "end": v(15, -98) * mm});
            skLineSegment(sketch, "E94.MirrorCS", {"start": v(15, -98) * mm, "end": v(33, -80) * mm});
            skCircle(sketch, "E95.MirrorC", {"center": v(0, -110) * mm, "radius": 6 * mm});
            skSolve(sketch);
        }
        {
            var Q0;
            Q0=makeQuery(id+"F16.imprint","IMPRINT",FACE,{"disambiguationData":[TD([[makeQuery(id+"F16.imprint","IMPRINT",EDGE,{"derivedFrom":sQuery(id+"F16.wireOp",EDGE,"E80")}),-1.0]])]});
            var Q1;
            {var subQ0=sQuery(id+"F16.wireOp",EDGE,"E90.MirrorCS");Q1=makeQuery(id+"F16.imprint","IMPRINT",FACE,{"disambiguationData":[TD([[makeQuery(id+"F16.imprint","IMPRINT",EDGE,{"derivedFrom":subQ0}),-1.0]])]});}
            var Q2;
            Q2=makeQuery(id+"F2.opExtrude","CAP_FACE",FACE,{"disambiguationData":[OSD([sQuery(id+"F0.wireOp",EDGE,"E12"),sQuery(id+"F0.wireOp",EDGE,"E13"),sQuery(id+"F0.wireOp",EDGE,"E14"),sQuery(id+"F0.wireOp",EDGE,"E15"),sQuery(id+"F0.wireOp",EDGE,"E17.filletArc"),sQuery(id+"F0.wireOp",EDGE,"E18.filletArc"),sQuery(id+"F0.wireOp",EDGE,"E19.filletArc"),sQuery(id+"F0.wireOp",EDGE,"E20.filletArc"),sQuery(id+"F0.wireOp",EDGE,"E25.0"),sQuery(id+"F0.wireOp",EDGE,"E25.1"),sQuery(id+"F0.wireOp",EDGE,"E25.2"),sQuery(id+"F0.wireOp",EDGE,"E25.3"),sQuery(id+"F0.wireOp",EDGE,"E25.4"),sQuery(id+"F0.wireOp",EDGE,"E25.5"),sQuery(id+"F0.wireOp",EDGE,"E25.6"),sQuery(id+"F0.wireOp",EDGE,"E25.7")])],"isStart":false});
            extrude(context, id + "F17", {"entities" : qUnion([Q0, Q1]), "endBound" : BoundingType.UP_TO_SURFACE, "depth" : 25 * mm, "endBoundEntityFace" : qUnion([Q2]), "offsetDistance" : 25 * mm});
        }
    });
